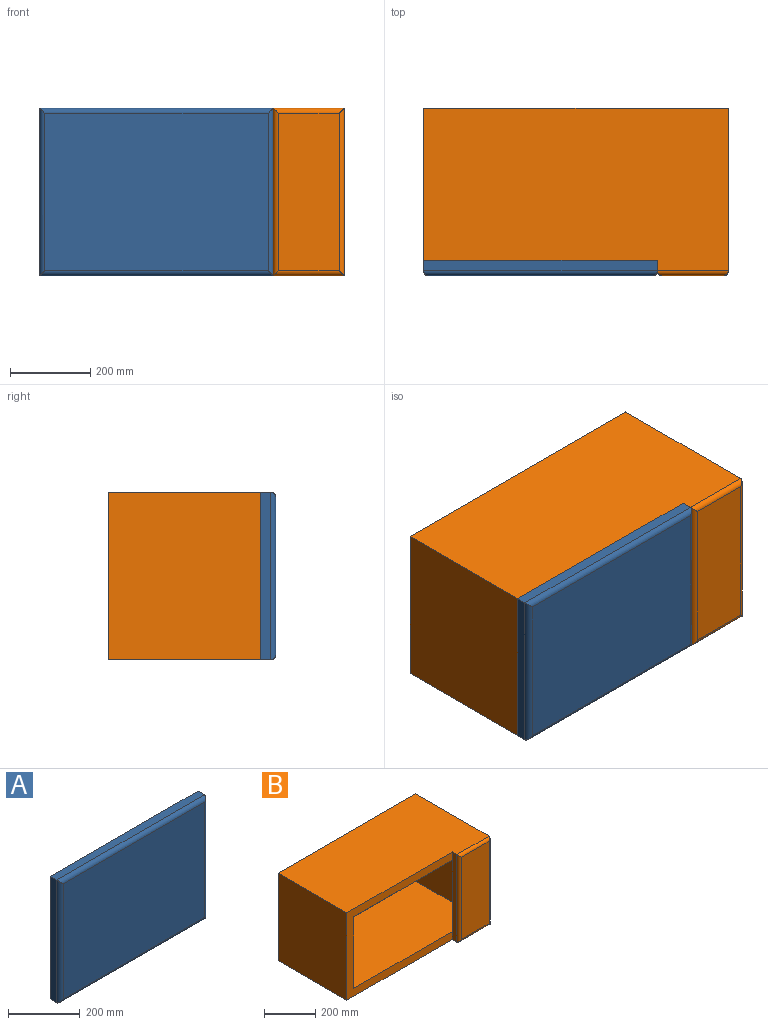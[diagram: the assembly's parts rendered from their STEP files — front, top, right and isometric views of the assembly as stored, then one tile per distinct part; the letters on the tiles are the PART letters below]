
ASSEMBLY  parts=2 mates=1
PART A: 10 faces, bbox 584.2x38.1x419.1 mm
  f0: plane 419.1x25.4mm, normal (1,0,0), area 10645.1mm2, adj f1,f3,f5,f6
  f1: plane 584.2x25.4mm, normal (0,0,1), area 14838.7mm2, adj f0,f2,f5,f8
  f2: plane 419.1x25.4mm, normal (-1,0,0), area 10645.1mm2, adj f1,f3,f5,f9
  f3: plane 584.2x25.4mm, normal (0,0,-1), area 14838.7mm2, adj f0,f2,f5,f7
  f4: plane 558.8x393.7mm, normal (0,-1,0), area 219999.6mm2, adj f6,f7,f8,f9
  f5: plane 584.2x419.1mm, normal (0,1,0), area 244838.2mm2, adj f0,f1,f2,f3
  f6: cylinder r=12.7mm len=419.1mm, axis (0,0,-1), area 8176.5mm2, adj f0,f4,f7,f8
  f7: cylinder r=12.7mm len=584.2mm, axis (-1,0,0), area 11470.1mm2, adj f3,f4,f6,f9
  f8: cylinder r=12.7mm len=584.2mm, axis (1,0,0), area 11470.1mm2, adj f1,f4,f6,f9
  f9: cylinder r=12.7mm len=419.1mm, axis (0,0,1), area 8176.5mm2, adj f2,f4,f7,f8
PART B: 18 faces, bbox 762x419.1x419.1 mm
  f0: plane 584.2x419.1mm, normal (0,-1,0), area 57580.5mm2, adj f2,f4,f5,f6,f14,f16,f17
  f1: plane 419.1x406.4mm, normal (1,0,0), area 170322.2mm2, adj f3,f4,f5,f9
  f2: plane 419.1x381mm, normal (-1,0,0), area 159677.1mm2, adj f0,f3,f4,f5
  f3: plane 762x419.1mm, normal (0,1,0), area 319354.2mm2, adj f1,f2,f4,f5
  f4: plane 762x406.4mm, normal (0,0,-1), area 294838.1mm2, adj f0,f1,f2,f3,f6,f11
  f5: plane 762x406.4mm, normal (0,0,1), area 294838.1mm2, adj f0,f1,f2,f3,f6,f8
  f6: plane 419.1x25.4mm, normal (-1,0,0), area 10645.1mm2, adj f0,f4,f5,f10,f12
  f7: plane 393.7x152.4mm, normal (0,-1,0), area 59999.9mm2, adj f8,f9,f10,f11
  f8: cylinder r=12.7mm len=177.8mm, axis (1,0,0), area 3362.8mm2, adj f5,f7,f9,f10
  f9: cylinder r=12.7mm len=419.1mm, axis (0,0,-1), area 8176.5mm2, adj f1,f7,f8,f11
  f10: cylinder r=12.7mm len=419.1mm, axis (0,0,1), area 8176.5mm2, adj f6,f7,f8,f11
  f11: cylinder r=12.7mm len=177.8mm, axis (-1,0,0), area 3362.8mm2, adj f4,f7,f9,f10
  f12: plane 342.9x139.7mm, normal (0,1,0), area 47903.1mm2, adj f6,f13,f16,f17
  f13: plane 342.9x342.9mm, normal (-1,0,0), area 117580.4mm2, adj f12,f15,f16,f17
  f14: plane 342.9x342.9mm, normal (1,0,0), area 117580.4mm2, adj f0,f15,f16,f17
  f15: plane 685.8x342.9mm, normal (0,-1,0), area 235160.8mm2, adj f13,f14,f16,f17
  f16: plane 685.8x342.9mm, normal (0,0,1), area 235160.8mm2, adj f0,f12,f13,f14,f15
  f17: plane 685.8x342.9mm, normal (0,0,-1), area 235160.8mm2, adj f0,f12,f13,f14,f15
PLACE A rot(axis=(0,0,-1),0deg) t=(0,0,0)mm
PLACE B at identity fixed
MATE revolute B.f5 <-> A.f1  axis (0,0,1) through (-1780.54,3924.3,1828.8)mm
